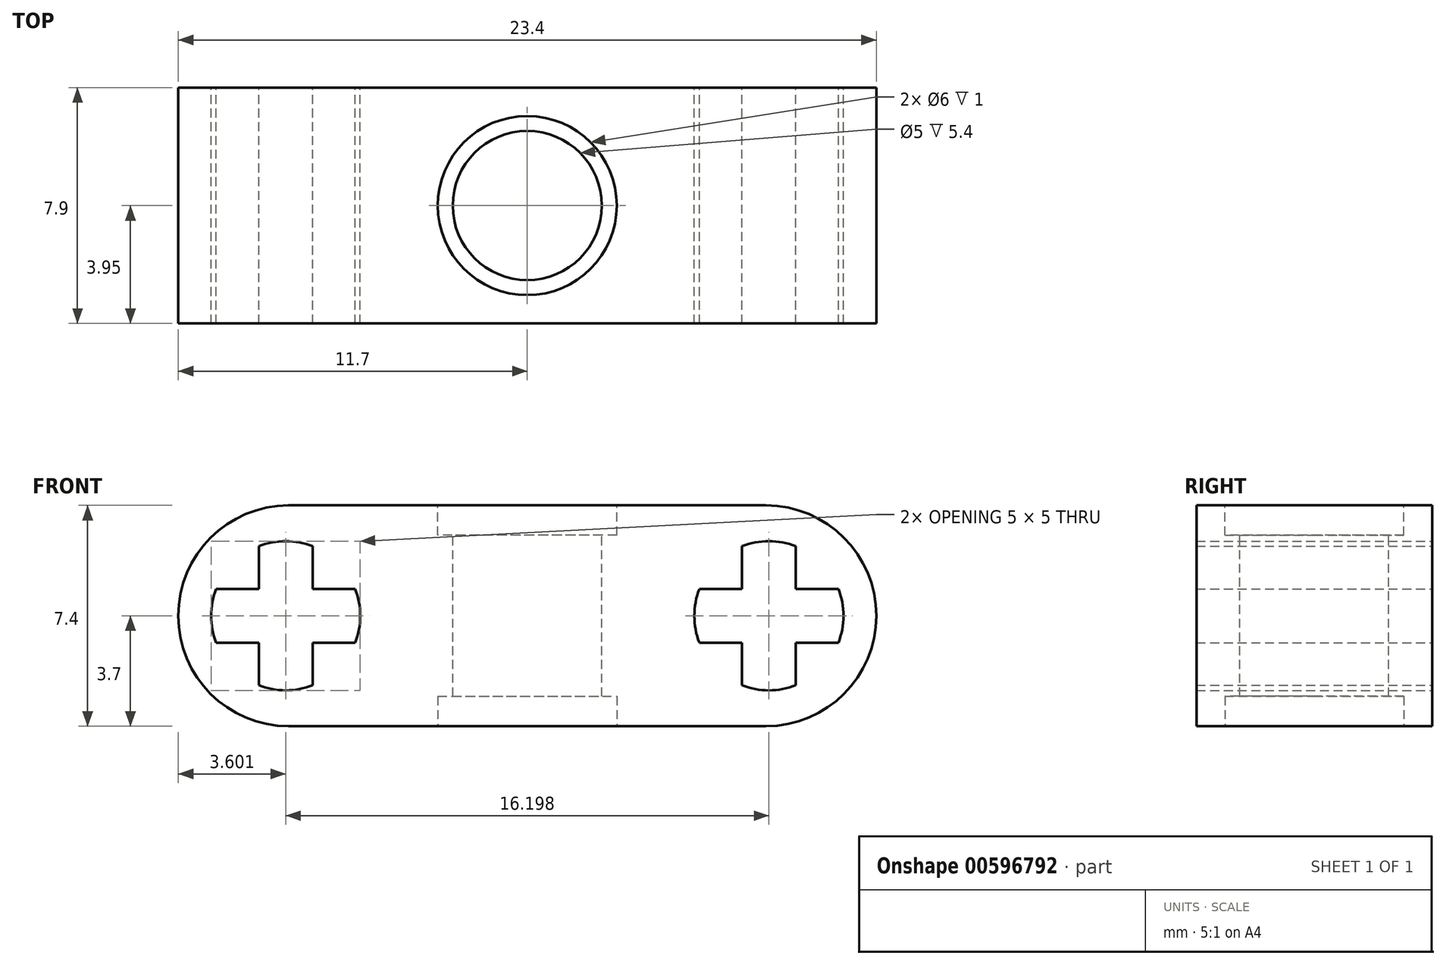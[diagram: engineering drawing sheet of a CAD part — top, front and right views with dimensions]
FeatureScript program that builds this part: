
annotation { "Feature Type Name" : "Feature", "Feature Type Description" : "" }
export const myFeature = defineFeature(function(context is Context, id is Id, definition is map)
    precondition{}
    {
        {
            var Q0;
            Q0=qCreatedBy(makeId("Front.planeOp"),FACE);
            var sketch = newSketch(context, id + "F0", { "sketchPlane" : qUnion([Q0])});
            skLineSegment(sketch, "E0.bottom", {"start": v(11.7, 3.7) * mm, "end": v(-11.7, 3.7) * mm});
            skLineSegment(sketch, "E0.top", {"start": v(11.7, -3.7) * mm, "end": v(-11.7, -3.7) * mm});
            skLineSegment(sketch, "E0.left", {"start": v(11.7, 3.7) * mm, "end": v(11.7, -3.7) * mm});
            skLineSegment(sketch, "E0.right", {"start": v(-11.7, 3.7) * mm, "end": v(-11.7, -3.7) * mm});
            skPoint(sketch, "E0.middle", {"position": v(0, 0) * mm});
            skArc(sketch, "E1", {"start": v(-9, -2.33) * mm, "mid": v(-8.1, -2.5) * mm, "end": v(-7.2, -2.33) * mm});
            skLineSegment(sketch, "E2.left", {"start": v(-7.2, 2.33) * mm, "end": v(-7.2, 0.9) * mm});
            skLineSegment(sketch, "E2.right", {"start": v(-9, 2.33) * mm, "end": v(-9, 0.9) * mm});
            skLineSegment(sketch, "E3.bottom", {"start": v(-5.77, 0.9) * mm, "end": v(-7.2, 0.9) * mm});
            skLineSegment(sketch, "E3.top", {"start": v(-5.77, -0.9) * mm, "end": v(-7.2, -0.9) * mm});
            skPoint(sketch, "E2.top.start.orphan", {"position": v(-7.2, -2.9) * mm});
            skPoint(sketch, "E4.orphan", {"position": v(-9, -2.9) * mm});
            skArc(sketch, "E5.trimOffspring", {"start": v(-10.43, 0.9) * mm, "mid": v(-10.6, 0) * mm, "end": v(-10.43, -0.9) * mm});
            skPoint(sketch, "E2.bottom.end.orphan", {"position": v(-9, 2.9) * mm});
            skPoint(sketch, "E6.orphan", {"position": v(-7.2, 2.9) * mm});
            skArc(sketch, "E7.trimOffspring", {"start": v(-7.2, 2.33) * mm, "mid": v(-8.1, 2.5) * mm, "end": v(-9, 2.33) * mm});
            skArc(sketch, "E8.trimOffspring", {"start": v(-5.77, -0.9) * mm, "mid": v(-5.6, 0) * mm, "end": v(-5.77, 0.9) * mm});
            skPoint(sketch, "E9.orphan", {"position": v(-5.6, -0.9) * mm});
            skPoint(sketch, "E10.orphan", {"position": v(-5.6, 0.9) * mm});
            skLineSegment(sketch, "E11.trimOffspring", {"start": v(-9, 0.9) * mm, "end": v(-10.43, 0.9) * mm});
            skLineSegment(sketch, "E12.trimOffspring", {"start": v(-9, -0.9) * mm, "end": v(-9, -2.33) * mm});
            skLineSegment(sketch, "E13.trimOffspring", {"start": v(-9, -0.9) * mm, "end": v(-10.43, -0.9) * mm});
            skLineSegment(sketch, "E14.trimOffspring", {"start": v(-7.2, -0.9) * mm, "end": v(-7.2, -2.33) * mm});
            skPoint(sketch, "E15.orphan", {"position": v(-10.6, 0.9) * mm});
            skPoint(sketch, "E16.orphan", {"position": v(-10.6, -0.9) * mm});
            skLineSegment(sketch, "E17", {"start": v(0, 5.75) * mm, "end": v(0, -6.04) * mm, "construction": true});
            skPoint(sketch, "E17.startSnap0", {"position": v(0, 3.7) * mm});
            skLineSegment(sketch, "E18.MirrorCS", {"start": v(7.2, 2.33) * mm, "end": v(7.2, 0.9) * mm});
            skArc(sketch, "E19.MirrorCS", {"start": v(7.2, 2.33) * mm, "mid": v(8.1, 2.5) * mm, "end": v(9, 2.33) * mm});
            skLineSegment(sketch, "E20.MirrorCS", {"start": v(9, 2.33) * mm, "end": v(9, 0.9) * mm});
            skLineSegment(sketch, "E21.MirrorCS", {"start": v(9, 0.9) * mm, "end": v(10.43, 0.9) * mm});
            skArc(sketch, "E22.MirrorCS", {"start": v(10.43, 0.9) * mm, "mid": v(10.6, 0) * mm, "end": v(10.43, -0.9) * mm});
            skLineSegment(sketch, "E23.MirrorCS", {"start": v(9, -0.9) * mm, "end": v(10.43, -0.9) * mm});
            skLineSegment(sketch, "E24.MirrorCS", {"start": v(9, -0.9) * mm, "end": v(9, -2.33) * mm});
            skArc(sketch, "E25.MirrorCS", {"start": v(9, -2.33) * mm, "mid": v(8.1, -2.5) * mm, "end": v(7.2, -2.33) * mm});
            skLineSegment(sketch, "E26.MirrorCS", {"start": v(7.2, -0.9) * mm, "end": v(7.2, -2.33) * mm});
            skLineSegment(sketch, "E27.MirrorCS", {"start": v(5.77, -0.9) * mm, "end": v(7.2, -0.9) * mm});
            skArc(sketch, "E28.MirrorCS", {"start": v(5.77, -0.9) * mm, "mid": v(5.6, 0) * mm, "end": v(5.77, 0.9) * mm});
            skLineSegment(sketch, "E29.MirrorCS", {"start": v(5.77, 0.9) * mm, "end": v(7.2, 0.9) * mm});
            skSolve(sketch);
        }
        {
            var Q0;
            Q0=qSketchRegion(id+"F0",true);
            extrude(context, id + "F1", {"entities" : qUnion([Q0]), "endBound" : BoundingType.SYMMETRIC, "depth" : 7.9 * mm, "offsetDistance" : 25 * mm});
        }
        {
            var Q0;
            Q0=makeQuery(id+"F1.opExtrude","SWEPT_EDGE",EDGE,{"disambiguationData":[OSD([sQuery(id+"F0.wireOp",EDGE,"E0.top"),sQuery(id+"F0.wireOp",EDGE,"E0.right")])]});
            var Q1;
            Q1=makeQuery(id+"F1.opExtrude","SWEPT_EDGE",EDGE,{"disambiguationData":[OSD([sQuery(id+"F0.wireOp",EDGE,"E0.bottom"),sQuery(id+"F0.wireOp",EDGE,"E0.right")])]});
            var Q2;
            Q2=makeQuery(id+"F1.opExtrude","SWEPT_EDGE",EDGE,{"disambiguationData":[OSD([sQuery(id+"F0.wireOp",EDGE,"E0.bottom"),sQuery(id+"F0.wireOp",EDGE,"E0.left")])]});
            var Q3;
            Q3=makeQuery(id+"F1.opExtrude","SWEPT_EDGE",EDGE,{"disambiguationData":[OSD([sQuery(id+"F0.wireOp",EDGE,"E0.top"),sQuery(id+"F0.wireOp",EDGE,"E0.left")])]});
            fillet(context, id + "F2", {"entities" : qUnion([Q0, Q1, Q2, Q3]), "radius" : 3.7 * mm, "tangentPropagation" : true, "allowEdgeOverflow" : false});
        }
        {
            var Q0;
            Q0=makeQuery(id+"F1.opExtrude","SWEPT_FACE",FACE,{"disambiguationData":[OSD([sQuery(id+"F0.wireOp",EDGE,"E0.bottom")])]});
            var sketch = newSketch(context, id + "F3", { "sketchPlane" : qUnion([Q0])});
            skCircle(sketch, "E30", {"center": v(0, 0) * mm, "radius": 2.5 * mm});
            skCircle(sketch, "E31", {"center": v(0, 0) * mm, "radius": 3 * mm});
            skSolve(sketch);
        }
        {
            var Q0;
            Q0=makeQuery(id+"F3.imprint","IMPRINT",FACE,{"disambiguationData":[TD([[makeQuery(id+"F3.imprint","IMPRINT",EDGE,{"derivedFrom":sQuery(id+"F3.wireOp",EDGE,"E30")}),1.0]])]});
            extrude(context, id + "F4", {"entities" : qUnion([Q0]), "operationType" : NewBodyOperationType.REMOVE, "oppositeDirection" : true, "depth" : 25 * mm, "offsetDistance" : 25 * mm});
        }
        {
            var Q0;
            Q0=makeQuery(id+"F3.imprint","IMPRINT",FACE,{"disambiguationData":[TD([[makeQuery(id+"F3.imprint","IMPRINT",EDGE,{"derivedFrom":sQuery(id+"F3.wireOp",EDGE,"E30")}),-1.0]])]});
            extrude(context, id + "F5", {"entities" : qUnion([Q0]), "operationType" : NewBodyOperationType.REMOVE, "oppositeDirection" : true, "depth" : 1 * mm, "offsetDistance" : 25 * mm});
        }
        {
            var Q0;
            Q0=makeQuery(id+"F1.opExtrude","SWEPT_FACE",FACE,{"disambiguationData":[OSD([sQuery(id+"F0.wireOp",EDGE,"E0.top")])]});
            var sketch = newSketch(context, id + "F6", { "sketchPlane" : qUnion([Q0])});
            skCircle(sketch, "E32", {"center": v(0, 0) * mm, "radius": 3 * mm});
            skSolve(sketch);
        }
        {
            var Q0;
            Q0=makeQuery(id+"F6.imprint","IMPRINT",FACE,{"disambiguationData":[TD([[makeQuery(id+"F6.imprint","IMPRINT",EDGE,{"derivedFrom":sQuery(id+"F6.wireOp",EDGE,"E32")}),1.0]])]});
            extrude(context, id + "F7", {"entities" : qUnion([Q0]), "operationType" : NewBodyOperationType.REMOVE, "oppositeDirection" : true, "depth" : 1 * mm, "offsetDistance" : 25 * mm});
        }
    });
